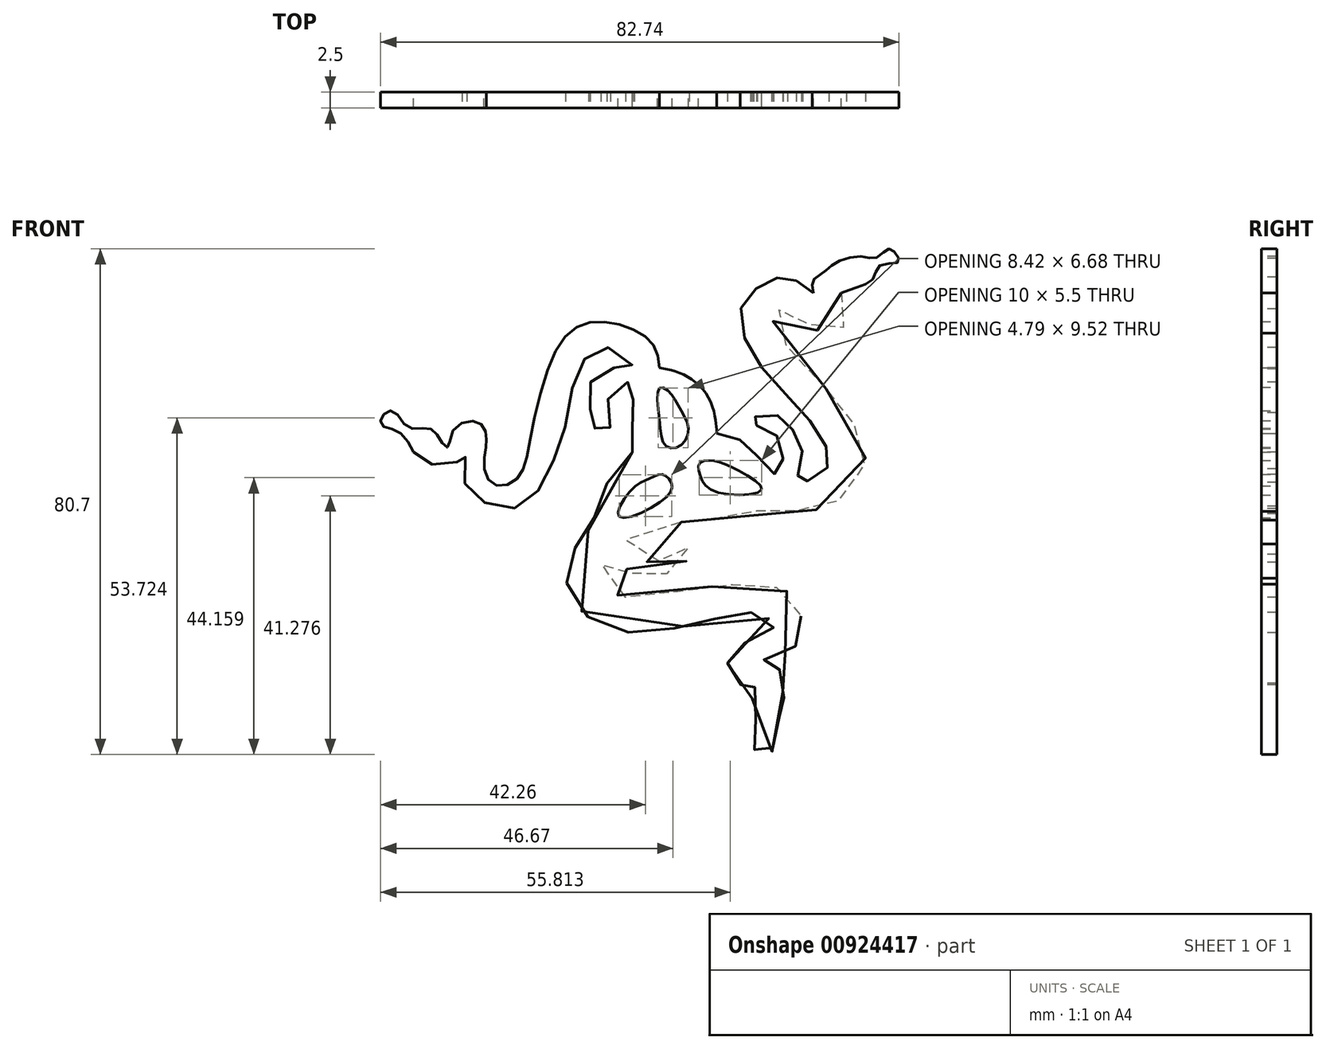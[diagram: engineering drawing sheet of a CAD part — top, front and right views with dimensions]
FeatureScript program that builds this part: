
annotation { "Feature Type Name" : "Feature", "Feature Type Description" : "" }
export const myFeature = defineFeature(function(context is Context, id is Id, definition is map)
    precondition{}
    {
        {
            var Q0;
            Q0=qCreatedBy(makeId("Front.planeOp"),FACE);
            var sketch = newSketch(context, id + "F0", { "sketchPlane" : qUnion([Q0])});
            skFitSpline(sketch, "E0", {"points": [v(11.09, 4.8) * mm, v(10.26, 8.2) * mm, v(7.5, 10.59) * mm, v(2.37, 12.15) * mm, v(-2.4, 11.14) * mm, v(-6.44, 5.36) * mm, v(-9.75, -7.58) * mm, v(-11.03, -12.08) * mm, v(-13.32, -13.92) * mm, v(-15.9, -13.46) * mm, v(-16.9, -10.7) * mm, v(-16.63, -7.86) * mm], "startDerivative": vector(-5.33, 45.68) * mm, "endDerivative": vector(6.8, 38.3) * mm});
            skFitSpline(sketch, "E1", {"points": [v(11.09, 4.8) * mm, v(14.95, 3.71) * mm, v(18.95, 0) * mm, v(20.15, -4.38) * mm, v(20.25, -5.67) * mm], "startDerivative": vector(14.55, -2.58) * mm, "endDerivative": vector(0.38, -7.26) * mm});
            skFitSpline(sketch, "E2", {"points": [v(20.25, -5.67) * mm, v(24.14, -6.77) * mm, v(26.93, -9.57) * mm, v(29.83, -12.16) * mm, v(30.83, -9.17) * mm, v(29.43, -5.67) * mm, v(26.14, -4.18) * mm, v(25.64, -3.58) * mm, v(28.63, -2.38) * mm, v(31.23, -3.88) * mm, v(33.33, -6.57) * mm, v(33.72, -11.07) * mm, v(33.03, -13.36) * mm, v(36.72, -12.36) * mm, v(38.12, -9.97) * mm, v(36.62, -5.67) * mm, v(30.83, 1.02) * mm, v(25.44, 7.9) * mm, v(24.14, 14.5) * mm, v(27.03, 17.79) * mm, v(30.43, 19.29) * mm, v(33.03, 18.69) * mm, v(35.62, 16.8) * mm], "startDerivative": vector(90.68, -15.87) * mm, "endDerivative": vector(61.4, -51.09) * mm});
            skFitSpline(sketch, "E3", {"points": [v(35.62, 16.8) * mm, v(35.62, 18.79) * mm, v(37.32, 20.09) * mm, v(39.02, 21.48) * mm, v(43.11, 22.58) * mm, v(45.7, 22.38) * mm, v(47.6, 23.78) * mm, v(48.8, 23.08) * mm, v(49.2, 21.68) * mm, v(46.3, 21.18) * mm, v(45.2, 19.09) * mm, v(42.61, 17.7) * mm, v(40.11, 16.8) * mm], "startDerivative": vector(-5.97, 28.87) * mm, "endDerivative": vector(-26.89, -10.18) * mm});
            skFitSpline(sketch, "E4", {"points": [v(40.11, 16.8) * mm, v(40.91, 13.6) * mm, v(40.11, 10.9) * mm, v(36.42, 10.7) * mm, v(34.02, 12.7) * mm, v(31.33, 14.2) * mm, v(29.23, 13.2) * mm, v(30.93, 8.8) * mm, v(34.72, 4.8) * mm, v(40.11, -1.58) * mm, v(43.01, -5.67) * mm, v(43.9, -10.07) * mm, v(41.21, -14.96) * mm, v(38.32, -17.16) * mm, v(33.23, -18.05) * mm, v(29.63, -17.26) * mm, v(24.94, -18.75) * mm, v(21.04, -19.45) * mm, v(17.15, -18.45) * mm, v(13.95, -20.05) * mm, v(5.77, -22.55) * mm, v(8.68, -26.02) * mm, v(12.45, -25.05) * mm, v(15.25, -23.35) * mm, v(15.77, -25.24) * mm, v(13.17, -27.71) * mm, v(9.46, -28.69) * mm, v(6.73, -28.1) * mm, v(3.02, -24.98) * mm, v(1.85, -29.14) * mm, v(5.1, -31.68) * mm, v(11.09, -31.3) * mm, v(20.25, -29.99) * mm, v(24.75, -29.73) * mm, v(29.89, -30.25) * mm, v(32.88, -32.2) * mm, v(33.73, -36.89) * mm, v(31.52, -40.66) * mm, v(27.35, -41.96) * mm, v(30.3, -43.42) * mm, v(30.84, -47.45) * mm, v(31.5, -49.06) * mm, v(29.09, -52.96) * mm, v(28.95, -56.58) * mm, v(26.4, -56.31) * mm, v(26.54, -52.69) * mm, v(26, -46.77) * mm, v(26.67, -45.57) * mm, v(23.58, -45.7) * mm, v(21.97, -42.6) * mm, v(22.9, -39.79) * mm, v(29.09, -37.37) * mm, v(27.88, -34.68) * mm, v(22.5, -34.68) * mm, v(14.98, -36.43) * mm, v(4.9, -37.23) * mm, v(-2.36, -32.8) * mm, v(-3.56, -26.08) * mm, v(0, -20.7) * mm, v(2.08, -14.8) * mm, v(6.78, -8.61) * mm], "startDerivative": vector(73.64, -218) * mm, "endDerivative": vector(253.07, 271.83) * mm});
            skFitSpline(sketch, "E5", {"points": [v(6.78, -8.61) * mm, v(6.78, -5.67) * mm, v(6.78, -1.09) * mm, v(6.78, 2.4) * mm, v(3.83, 1.33) * mm, v(2.75, -2.43) * mm, v(3.02, -5.67) * mm, v(0, -4.04) * mm, v(0, -1.9) * mm, v(0, 2.27) * mm, v(3.42, 4.8) * mm, v(6.78, 4.8) * mm, v(3.96, 7.78) * mm, v(0, 7.1) * mm, v(-2.49, 2.94) * mm, v(-4.24, -5.67) * mm, v(-6.79, -11.97) * mm, v(-10.28, -16.94) * mm, v(-15.26, -17.35) * mm, v(-19.29, -14.66) * mm, v(-20.36, -11.03) * mm, v(-19.69, -8.61) * mm, v(-22.65, -11.17) * mm, v(-25.87, -10.1) * mm, v(-28.15, -8.61) * mm], "startDerivative": vector(1.7, 78.8) * mm, "endDerivative": vector(-63.5, 38.53) * mm});
            skFitSpline(sketch, "E6", {"points": [v(-16.63, -7.86) * mm, v(-16.63, -5.64) * mm, v(-17.94, -3.81) * mm, v(-21.7, -4.95) * mm, v(-22.72, -7.86) * mm, v(-23.98, -6.55) * mm, v(-25.69, -4.84) * mm, v(-28.99, -4.72) * mm, v(-31.38, -2.1) * mm, v(-33.1, -2.79) * mm, v(-33.2, -4.38) * mm, v(-30.7, -5.3) * mm, v(-28.15, -8.61) * mm], "startDerivative": vector(2.8, 29.16) * mm, "endDerivative": vector(20.43, -39.4) * mm});
            skFitSpline(sketch, "E7", {"points": [v(11.09, 1.6) * mm, v(11.09, -3.78) * mm, v(12.11, -7.68) * mm, v(14.32, -7.68) * mm, v(15.7, -5.04) * mm, v(14.43, -1.78) * mm, v(12.64, 0.96) * mm, v(11.09, 1.6) * mm]});
            skFitSpline(sketch, "E8", {"points": [v(27.4, -14.63) * mm, v(22.86, -11.16) * mm, v(19.49, -10) * mm, v(17.49, -10.42) * mm, v(17.6, -12.42) * mm, v(20.01, -14.95) * mm, v(27.4, -14.63) * mm]});
            skFitSpline(sketch, "E9", {"points": [v(4.63, -18.95) * mm, v(6.84, -14.42) * mm, v(9.8, -12.74) * mm, v(11.58, -12.2) * mm, v(12.95, -13.47) * mm, v(12, -16) * mm, v(4.63, -18.95) * mm]});
            skSolve(sketch);
        }
        {
            var Q0;
            Q0 = qSketchRegion(id + "F0", true);
            extrude(context, id + "F1", {"entities" : qUnion([Q0]), "depth" : 2.5 * mm, "offsetDistance" : 25.4 * mm});
        }
    });
